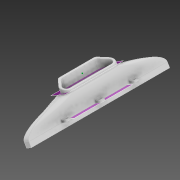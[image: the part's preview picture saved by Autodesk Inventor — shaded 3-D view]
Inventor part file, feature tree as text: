
AUTODESK INVENTOR PART (.ipt)
format: ipt  version: 2020 (Build 240168000, 168)  size: 976,384 bytes
history: native  units: in
note: dims shown in document units (in); Inventor stores cm internally (conversion verified against a paired STEP export)
features: sketch x13, extrude x9, fillet x6, other x4, loft x3, plane x2, mirror x1, pattern_linear x1
ambient origin geometry x8: Origin, YZ Plane, XZ Plane, XY Plane, X Axis, Y Axis, Z Axis, Center Point
bodies: Solid1 (feature_tree)
feature tree (39):
  extrude  "Extrusion1"  Depth=0.3543in
  fillet  "Fillet1"  Radius=0.3543in
  fillet  "Fillet2"  Radius=1.0236in
  plane  "Work Plane1"
  extrude  "Extrusion2"  Depth=1.0236in
  fillet  "Fillet3"  Radius=1.6555in
  fillet  "Fillet4"  Radius=0.4724in
  loft  "Loft1"
  mirror  "Mirror4"
  extrude  "Extrusion3"  Depth=0.1181in
  extrude  "Extrusion4"  Depth=0.1181in
  extrude  "Extrusion5"  TaperAngle=0.0deg  [1 undecoded]
  extrude  "Extrusion6"  Depth=0.0787in TaperAngle=0.0deg
  extrude  "Extrusion7"  Depth=0.315in
  plane  "Work Plane2"
  loft  "Loft4"
  loft  "Loft5"
  extrude  "Extrusion10"  Depth=0.0394in TaperAngle=0.0deg
  sketch  "Sketch13"  dims[d49=0.0394in d50=0.0in d51=0.0394in d52=0.0in]
  extrude  "Extrusion11"  Depth=0.9843in
  fillet  "Fillet6"  Radius=0.0787in
  pattern_linear  "Rectangular Pattern1"  Spacing1=0.0787in  [1 undecoded]
  sketch  "Sketch15"  dims[d58=0.1575in d59=0.0787in d60=0.0787in d61=0.315in d90=0.0787in d91=0.0787in d93=0.0787in d94=7.874in d102=0.0in d103=90.0deg d106=0.1575in d107=7.874in d112=0.3937in d113=90.0deg d114=0.0in d115=90.0deg d116=0.0in d117=90.0deg d118=0.2756in d119=0.0in d120=3.937in d121=1.9685in d122=0.1575in d123=0.315in d124=0.3937in d125=0.1575in d126=0.1575in d127=0.0984in d128=0.0in d129=0.0787in d130=1.1811in d132=1.9685in d134=0.0787in]
  fillet  "Fillet8"  Radius=0.0787in
  sketch  "Sketch1"  dims[d0=0.3543in d1=0.3543in d2=0.3543in d3=1.0236in]
  sketch  "Sketch3"  dims[d4=90.0deg d5=1.0236in d7=1.6555in d9=0.4724in]
  other  "Edges1"
  other  "Edges2"
  sketch  "Sketch4"  dims[d10=0.9449in d17=0.0394in d18=0.0in]
  sketch  "Sketch5"  dims[d19=0.1969in d21=0.1181in]
  sketch  "Sketch6"  dims[d22=0.315in d23=0.1181in]
  sketch  "Sketch7"  dims[d24=30.0deg d35=0.0in]
  sketch  "Sketch8"  dims[d36=0.1181in d37=0.0787in d38=0.0in]
  sketch  "Sketch10"  dims[d39=0.1969in d40=0.315in]
  sketch  "Sketch11"  dims[d41=0.0in d42=90.0deg d43=0.0in d44=90.0deg]
  other  "Edges13"
  sketch  "Sketch12"  dims[d45=0.0787in d46=0.0in d47=0.0394in d48=0.0in]
  other  "Edges14"
  sketch  "Sketch14"  dims[d53=0.0394in d54=0.0in d55=0.9843in d57=0.0787in]
note: 2 required parameter values undecoded (feature->parameter linkage not recoverable at this tier; creation-order binding heuristic only, values carry confidence <= 0.55)
